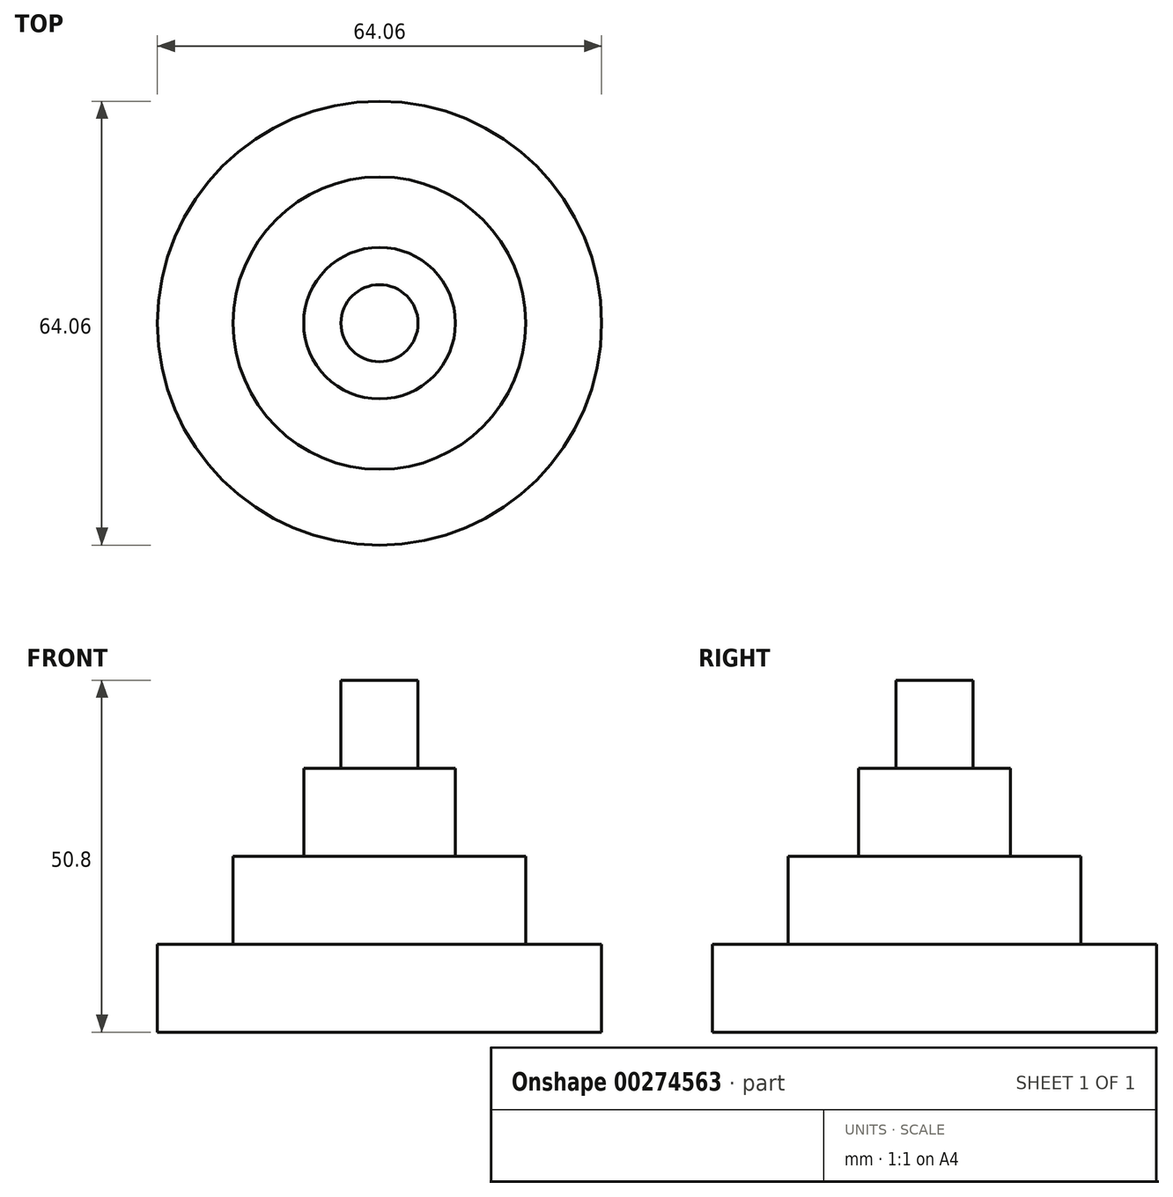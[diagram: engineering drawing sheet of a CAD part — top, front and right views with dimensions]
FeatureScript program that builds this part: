
annotation { "Feature Type Name" : "Feature", "Feature Type Description" : "" }
export const myFeature = defineFeature(function(context is Context, id is Id, definition is map)
    precondition{}
    {
        {
            var Q0;
            Q0=qCreatedBy(makeId("Top.planeOp"),FACE);
            var sketch = newSketch(context, id + "F0", { "sketchPlane" : qUnion([Q0])});
            skCircle(sketch, "E0", {"center": v(0, 0) * mm, "radius": 32.03 * mm});
            skCircle(sketch, "E1", {"center": v(0, 0) * mm, "radius": 21.1 * mm});
            skCircle(sketch, "E2", {"center": v(0, 0) * mm, "radius": 10.94 * mm});
            skCircle(sketch, "E3", {"center": v(0, 0) * mm, "radius": 5.55 * mm});
            skSolve(sketch);
        }
        {
            var Q0;
            Q0=makeQuery(id+"F0.imprint","IMPRINT",FACE,{"disambiguationData":[TD([[makeQuery(id+"F0.imprint","IMPRINT",EDGE,{"derivedFrom":sQuery(id+"F0.wireOp",EDGE,"E0")}),1.0]])]});
            extrude(context, id + "F1", {"entities" : qUnion([Q0]), "depth" : 12.7 * mm});
        }
        {
            var Q0;
            Q0=makeQuery(id+"F0.imprint","IMPRINT",FACE,{"disambiguationData":[TD([[makeQuery(id+"F0.imprint","IMPRINT",EDGE,{"derivedFrom":sQuery(id+"F0.wireOp",EDGE,"E1")}),1.0]])]});
            extrude(context, id + "F2", {"entities" : qUnion([Q0]), "operationType" : NewBodyOperationType.ADD, "depth" : 25.4 * mm});
        }
        {
            var Q0;
            Q0=makeQuery(id+"F0.imprint","IMPRINT",FACE,{"disambiguationData":[TD([[makeQuery(id+"F0.imprint","IMPRINT",EDGE,{"derivedFrom":sQuery(id+"F0.wireOp",EDGE,"E2")}),1.0]])]});
            extrude(context, id + "F3", {"entities" : qUnion([Q0]), "operationType" : NewBodyOperationType.ADD, "depth" : 38.1 * mm});
        }
        {
            var Q0;
            Q0=makeQuery(id+"F0.imprint","IMPRINT",FACE,{"disambiguationData":[TD([[makeQuery(id+"F0.imprint","IMPRINT",EDGE,{"derivedFrom":sQuery(id+"F0.wireOp",EDGE,"E3")}),1.0]])]});
            extrude(context, id + "F4", {"entities" : qUnion([Q0]), "operationType" : NewBodyOperationType.ADD, "depth" : 50.8 * mm});
        }
    });
